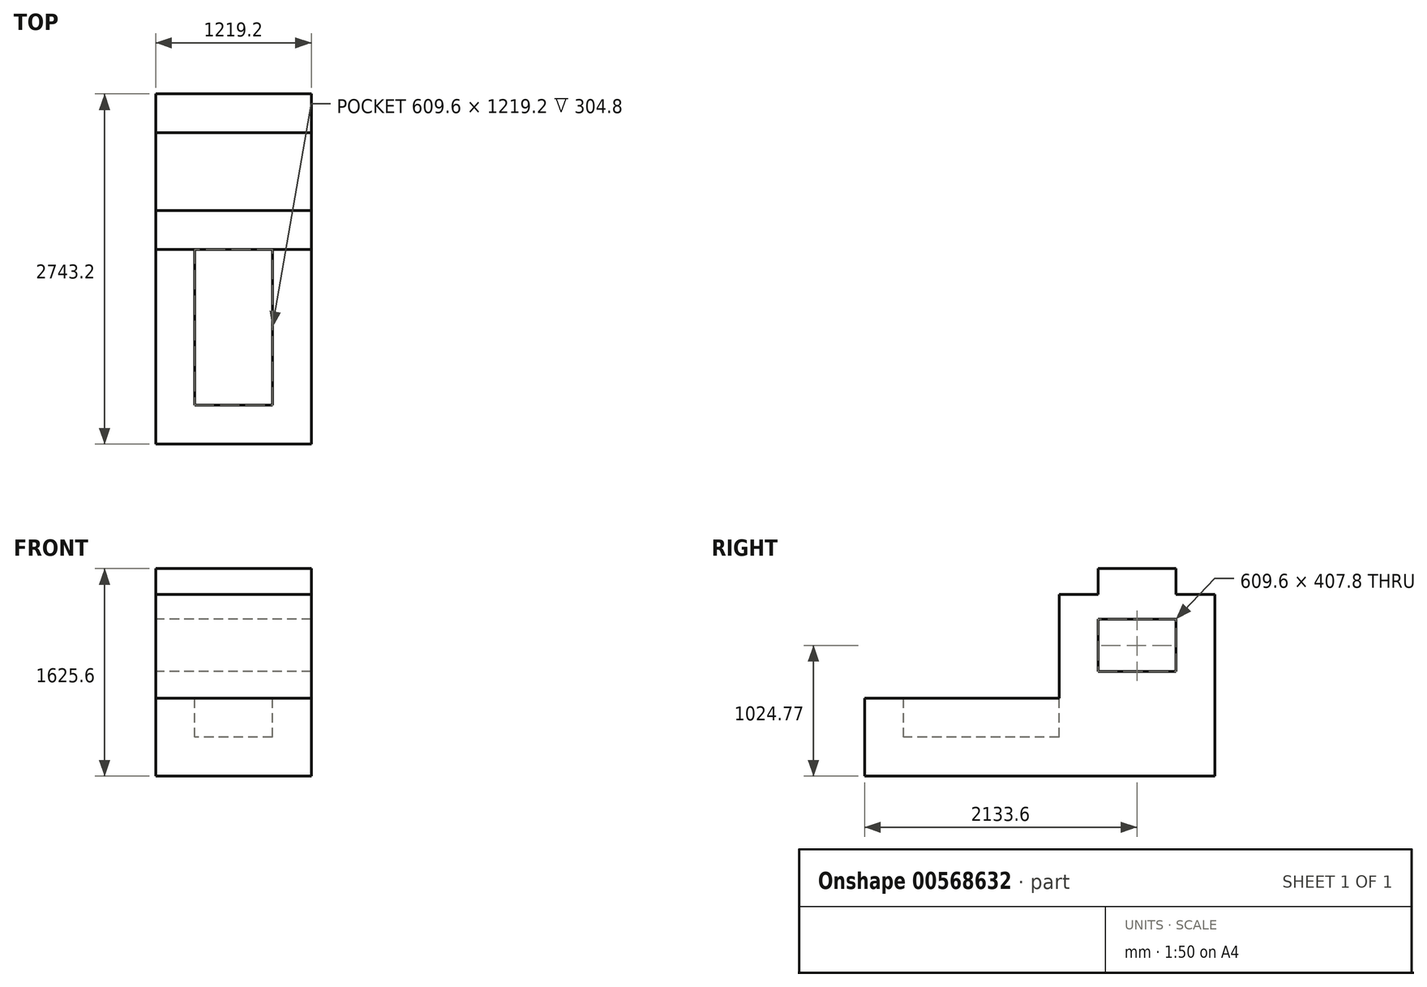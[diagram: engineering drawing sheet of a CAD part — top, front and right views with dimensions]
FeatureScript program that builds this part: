
annotation { "Feature Type Name" : "Feature", "Feature Type Description" : "" }
export const myFeature = defineFeature(function(context is Context, id is Id, definition is map)
    precondition{}
    {
        {
            var Q0;
            Q0=qCreatedBy(makeId("Right.planeOp"),FACE);
            var sketch = newSketch(context, id + "F0", { "sketchPlane" : qUnion([Q0])});
            skLineSegment(sketch, "E0", {"start": v(0, 0) * mm, "end": v(2743.2, 0) * mm});
            skLineSegment(sketch, "E1", {"start": v(2743.2, 0) * mm, "end": v(2743.2, 1422.4) * mm});
            skLineSegment(sketch, "E2", {"start": v(2743.2, 1422.4) * mm, "end": v(2438.4, 1422.4) * mm});
            skLineSegment(sketch, "E3", {"start": v(2438.4, 1422.4) * mm, "end": v(2438.4, 1625.6) * mm});
            skLineSegment(sketch, "E4", {"start": v(2438.4, 1625.6) * mm, "end": v(1828.8, 1625.6) * mm});
            skLineSegment(sketch, "E5", {"start": v(1828.8, 1625.6) * mm, "end": v(1828.8, 1422.4) * mm});
            skLineSegment(sketch, "E6", {"start": v(1828.8, 1422.4) * mm, "end": v(1524, 1422.4) * mm});
            skLineSegment(sketch, "E7", {"start": v(1524, 1422.4) * mm, "end": v(1524, 609.6) * mm});
            skLineSegment(sketch, "E8", {"start": v(1524, 609.6) * mm, "end": v(0, 609.6) * mm});
            skLineSegment(sketch, "E9", {"start": v(0, 609.6) * mm, "end": v(0, 0) * mm});
            skLineSegment(sketch, "E10", {"start": v(1828.8, 1228.67) * mm, "end": v(1828.8, 820.87) * mm});
            skLineSegment(sketch, "E11", {"start": v(1828.8, 820.87) * mm, "end": v(2438.4, 820.87) * mm});
            skLineSegment(sketch, "E12", {"start": v(2438.4, 820.87) * mm, "end": v(2438.4, 1228.67) * mm});
            skLineSegment(sketch, "E13", {"start": v(2438.4, 1228.67) * mm, "end": v(1828.8, 1228.67) * mm});
            skSolve(sketch);
        }
        {
            var Q0;
            Q0 = qSketchRegion(id + "F0", true);
            var Q1;
            Q1=makeQuery(id+"F0.imprint","IMPRINT",FACE,{"disambiguationData":[TD([[makeQuery(id+"F0.imprint","IMPRINT",EDGE,{"derivedFrom":sQuery(id+"F0.wireOp",EDGE,"E0")}),1.0]])]});
            extrude(context, id + "F1", {"entities" : qUnion([Q0, Q1]), "depth" : 1219.2 * mm, "offsetDistance" : 25.4 * mm});
        }
        {
            var Q0;
            Q0=makeQuery(id+"F1.opExtrude","SWEPT_FACE",FACE,{"disambiguationData":[OSD([sQuery(id+"F0.wireOp",EDGE,"E8")])]});
            var sketch = newSketch(context, id + "F2", { "sketchPlane" : qUnion([Q0])});
            skLineSegment(sketch, "E14", {"start": v(0, 1524) * mm, "end": v(304.8, 1524) * mm});
            skLineSegment(sketch, "E15", {"start": v(304.8, 1524) * mm, "end": v(304.8, 304.8) * mm});
            skLineSegment(sketch, "E16", {"start": v(304.8, 304.8) * mm, "end": v(914.4, 304.8) * mm});
            skLineSegment(sketch, "E17", {"start": v(914.4, 304.8) * mm, "end": v(914.4, 1524) * mm});
            skLineSegment(sketch, "E18", {"start": v(914.4, 1524) * mm, "end": v(304.8, 1524) * mm});
            skSolve(sketch);
        }
        {
            var Q0;
            Q0=makeQuery(id+"F2.imprint","IMPRINT",FACE,{"disambiguationData":[TD([[makeQuery(id+"F2.imprint","IMPRINT",EDGE,{"derivedFrom":sQuery(id+"F2.wireOp",EDGE,"E15")}),1.0]])]});
            extrude(context, id + "F3", {"entities" : qUnion([Q0]), "operationType" : NewBodyOperationType.REMOVE, "oppositeDirection" : true, "depth" : 304.8 * mm, "offsetDistance" : 25.4 * mm});
        }
    });
